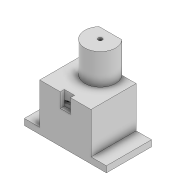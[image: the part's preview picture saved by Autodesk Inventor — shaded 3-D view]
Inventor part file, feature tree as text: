
AUTODESK INVENTOR PART (.ipt)
format: ipt  version: 2022 (Build 260153000, 153)  size: 181,248 bytes
history: native  units: mm
features: extrude x8, sketch x8, projected_geometry x2, thicken_offset x1
ambient origin geometry x8: Origin, YZ Plane, XZ Plane, XY Plane, X Axis, Y Axis, Z Axis, Center Point
bodies: Solid1 (feature_tree)
feature tree (19):
  extrude  "Extrusion1"  Depth=25.0mm
  extrude  "Extrusion2"  Depth=20.0mm TaperAngle=0.0deg
  extrude  "Extrusion3"  Depth=100.0mm TaperAngle=0.0deg
  extrude  "Extrusion4"  Depth=15.0mm TaperAngle=0.0deg
  thicken_offset  "Thicken1"
  extrude  "Extrusion5"  Depth=40.0mm
  extrude  "Extrusion6"  Depth=3.0mm
  extrude  "Extrusion7"  Depth=10.0mm
  extrude  "Extrusion8"  Depth=3.0mm TaperAngle=0.0deg
  sketch  "Sketch1"  dims[d0=12.2mm d1=25.0mm]
  sketch  "Sketch2"  dims[d2=20.0mm d3=20.0mm d4=0.0mm]
  sketch  "Sketch3"  dims[d5=2.0mm d6=100.0mm d7=0.0mm]
  projected_geometry  "Projected Loop1"
  sketch  "Sketch4"  dims[d8=15.0mm d9=15.0mm d10=0.0mm]
  sketch  "Sketch5"  dims[d11=30.0mm d12=40.0mm]
  projected_geometry  "Projected Loop2"
  sketch  "Sketch6"  dims[d13=3.0mm d14=0.0mm d15=5.0mm]
  sketch  "Sketch7"  dims[d16=5.0mm d17=10.0mm]
  sketch  "Sketch8"  dims[d18=10.0mm d19=2.0mm d20=0.0mm d21=10.0mm d22=0.0mm d23=9.8mm d24=22.0mm d25=0.0mm d26=100.0mm d27=0.0mm d28=3.0mm]
